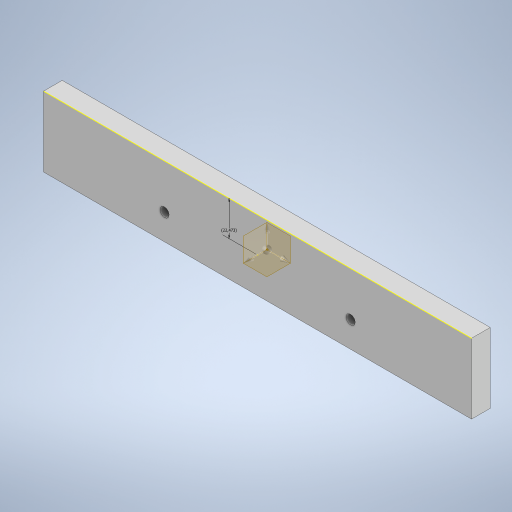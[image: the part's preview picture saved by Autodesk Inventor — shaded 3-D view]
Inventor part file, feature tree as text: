
AUTODESK INVENTOR PART (.ipt)
format: ipt  version: 2024 (Build 280153000, 153)  size: 231,936 bytes
history: native  units: mm
features: other x6, sketch x1
ambient origin geometry x8: Origin, YZ Plane, XZ Plane, XY Plane, X Axis, Y Axis, Z Axis, Center Point
bodies: Body1 (feature_tree)
feature tree (7):
  other  "BORDE_6"
  other  "Generador_de_Piezas.ipt"
  other  "Desplazar cuerpo1"
  sketch  "Boceto1"  dims[d0=10.0mm d1=-462.865mm d2=-2286.154mm d3=0.0mm d4=22.47274mm d5=0.0mm d6=-0.027mm d7=0.0mm]
  other  "Desplazar cuerpo2"
  other  "BORDE_6::Generador_de_Piezas.ipt"
  other  "OperaciónIdentificador1"
